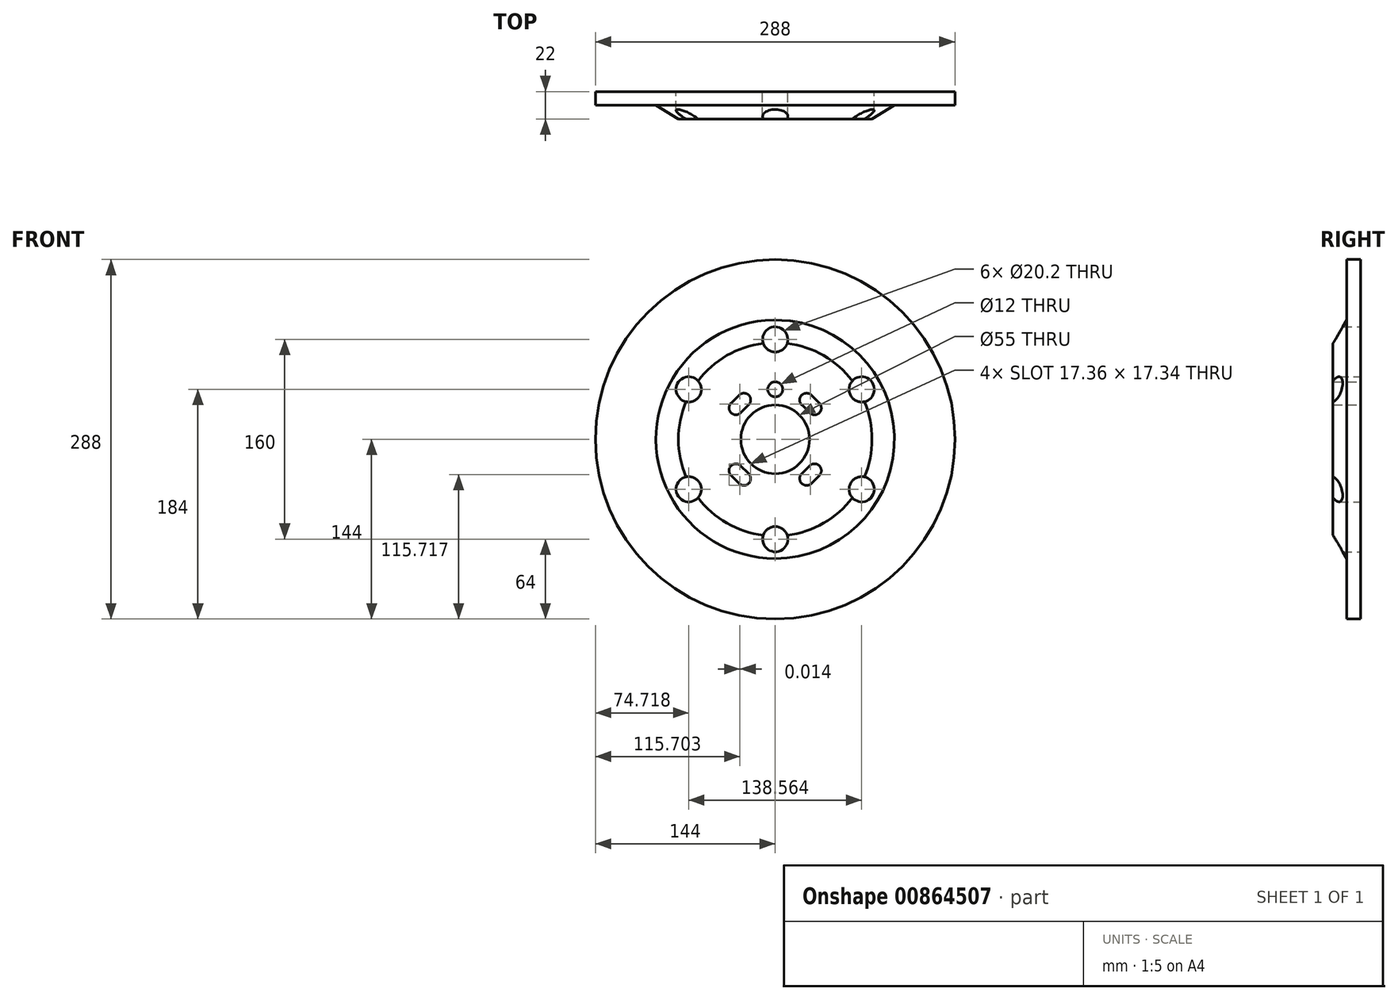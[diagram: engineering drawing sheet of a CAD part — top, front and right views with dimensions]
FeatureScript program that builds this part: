
annotation { "Feature Type Name" : "Feature", "Feature Type Description" : "" }
export const myFeature = defineFeature(function(context is Context, id is Id, definition is map)
    precondition{}
    {
        {
            var Q0;
            Q0=qCreatedBy(makeId("Front.planeOp"),FACE);
            var sketch = newSketch(context, id + "F0", { "sketchPlane" : qUnion([Q0])});
            skCircle(sketch, "E0", {"center": v(0, 0) * mm, "radius": 144 * mm});
            skCircle(sketch, "E1", {"center": v(0, 0) * mm, "radius": 27.5 * mm});
            skCircle(sketch, "E2", {"center": v(0, 80) * mm, "radius": 10.1 * mm});
            skCircle(sketch, "E3.1.0", {"center": v(-69.28, 40) * mm, "radius": 10.1 * mm});
            skCircle(sketch, "E3.2.0", {"center": v(-69.28, -40) * mm, "radius": 10.1 * mm});
            skCircle(sketch, "E3.3.0", {"center": v(0, -80) * mm, "radius": 10.1 * mm});
            skCircle(sketch, "E3.4.0", {"center": v(69.28, -40) * mm, "radius": 10.1 * mm});
            skCircle(sketch, "E3.5.0", {"center": v(69.28, 40) * mm, "radius": 10.1 * mm});
            skCircle(sketch, "E4", {"center": v(0, 40) * mm, "radius": 6 * mm});
            skLineSegment(sketch, "E5", {"start": v(0, 40) * mm, "end": v(9, 40) * mm, "construction": true});
            skLineSegment(sketch, "E6", {"start": v(0, 40) * mm, "end": v(-9, 40) * mm, "construction": true});
            skCircle(sketch, "E7.1.0", {"center": v(-25.1, 31.47) * mm, "radius": 5.5 * mm});
            skLineSegment(sketch, "E7.1.1", {"start": v(-35.35, 29) * mm, "end": v(-29, 35.36) * mm});
            skCircle(sketch, "E7.1.2", {"center": v(-31.47, 25.1) * mm, "radius": 5.5 * mm});
            skLineSegment(sketch, "E7.1.3", {"start": v(-28.15, 20.72) * mm, "end": v(-21.23, 27.56) * mm});
            skCircle(sketch, "E7.3.0", {"center": v(-31.47, -25.1) * mm, "radius": 5.5 * mm});
            skLineSegment(sketch, "E7.3.1", {"start": v(-29, -35.35) * mm, "end": v(-35.36, -29) * mm});
            skCircle(sketch, "E7.3.2", {"center": v(-25.1, -31.47) * mm, "radius": 5.5 * mm});
            skLineSegment(sketch, "E7.3.3", {"start": v(-20.72, -28.15) * mm, "end": v(-27.56, -21.23) * mm});
            skCircle(sketch, "E7.5.0", {"center": v(25.1, -31.47) * mm, "radius": 5.5 * mm});
            skLineSegment(sketch, "E7.5.1", {"start": v(35.35, -29) * mm, "end": v(29, -35.36) * mm});
            skCircle(sketch, "E7.5.2", {"center": v(31.47, -25.1) * mm, "radius": 5.5 * mm});
            skLineSegment(sketch, "E7.5.3", {"start": v(28.15, -20.72) * mm, "end": v(21.23, -27.56) * mm});
            skCircle(sketch, "E7.7.0", {"center": v(31.47, 25.1) * mm, "radius": 5.5 * mm});
            skLineSegment(sketch, "E7.7.1", {"start": v(29, 35.35) * mm, "end": v(35.36, 29) * mm});
            skCircle(sketch, "E7.7.2", {"center": v(25.1, 31.47) * mm, "radius": 5.5 * mm});
            skLineSegment(sketch, "E7.7.3", {"start": v(20.72, 28.15) * mm, "end": v(27.56, 21.23) * mm});
            skCircle(sketch, "E8.cCircle", {"center": v(0, 0) * mm, "radius": 125 * mm, "construction": true});
            skLineSegment(sketch, "E8.0", {"start": v(27.81, 121.86) * mm, "end": v(54.23, 112.61) * mm, "construction": true});
            skLineSegment(sketch, "E8.1", {"start": v(54.23, 112.61) * mm, "end": v(77.93, 97.72) * mm, "construction": true});
            skLineSegment(sketch, "E8.2", {"start": v(77.93, 97.72) * mm, "end": v(97.72, 77.93) * mm, "construction": true});
            skLineSegment(sketch, "E8.3", {"start": v(97.72, 77.93) * mm, "end": v(112.61, 54.23) * mm, "construction": true});
            skLineSegment(sketch, "E8.4", {"start": v(112.61, 54.23) * mm, "end": v(121.86, 27.81) * mm, "construction": true});
            skLineSegment(sketch, "E8.5", {"start": v(121.86, 27.81) * mm, "end": v(124.99, 0) * mm, "construction": true});
            skLineSegment(sketch, "E8.6", {"start": v(125, 0) * mm, "end": v(121.86, -27.81) * mm, "construction": true});
            skLineSegment(sketch, "E8.7", {"start": v(121.86, -27.81) * mm, "end": v(112.61, -54.23) * mm, "construction": true});
            skLineSegment(sketch, "E8.8", {"start": v(112.61, -54.23) * mm, "end": v(97.72, -77.93) * mm, "construction": true});
            skLineSegment(sketch, "E8.9", {"start": v(97.72, -77.93) * mm, "end": v(77.93, -97.72) * mm, "construction": true});
            skLineSegment(sketch, "E8.10", {"start": v(77.93, -97.72) * mm, "end": v(54.23, -112.61) * mm, "construction": true});
            skLineSegment(sketch, "E8.11", {"start": v(54.23, -112.61) * mm, "end": v(27.81, -121.86) * mm, "construction": true});
            skLineSegment(sketch, "E8.12", {"start": v(27.81, -121.86) * mm, "end": v(0, -125) * mm, "construction": true});
            skLineSegment(sketch, "E8.13", {"start": v(0, -125) * mm, "end": v(-27.81, -121.86) * mm, "construction": true});
            skLineSegment(sketch, "E8.14", {"start": v(-27.81, -121.86) * mm, "end": v(-54.23, -112.61) * mm, "construction": true});
            skLineSegment(sketch, "E8.15", {"start": v(-54.23, -112.61) * mm, "end": v(-77.93, -97.72) * mm, "construction": true});
            skLineSegment(sketch, "E8.16", {"start": v(-77.93, -97.72) * mm, "end": v(-97.72, -77.93) * mm, "construction": true});
            skLineSegment(sketch, "E8.17", {"start": v(-97.72, -77.93) * mm, "end": v(-112.61, -54.23) * mm, "construction": true});
            skLineSegment(sketch, "E8.18", {"start": v(-112.61, -54.23) * mm, "end": v(-121.86, -27.81) * mm, "construction": true});
            skLineSegment(sketch, "E8.19", {"start": v(-121.86, -27.81) * mm, "end": v(-124.99, 0) * mm, "construction": true});
            skLineSegment(sketch, "E8.20", {"start": v(-125, 0) * mm, "end": v(-121.86, 27.81) * mm, "construction": true});
            skLineSegment(sketch, "E8.21", {"start": v(-121.86, 27.81) * mm, "end": v(-112.61, 54.23) * mm, "construction": true});
            skLineSegment(sketch, "E8.22", {"start": v(-112.61, 54.23) * mm, "end": v(-97.72, 77.93) * mm, "construction": true});
            skLineSegment(sketch, "E8.23", {"start": v(-97.72, 77.93) * mm, "end": v(-77.93, 97.72) * mm, "construction": true});
            skLineSegment(sketch, "E8.24", {"start": v(-77.93, 97.72) * mm, "end": v(-54.23, 112.61) * mm, "construction": true});
            skLineSegment(sketch, "E8.25", {"start": v(-54.23, 112.61) * mm, "end": v(-27.81, 121.86) * mm, "construction": true});
            skLineSegment(sketch, "E8.26", {"start": v(-27.81, 121.86) * mm, "end": v(0, 125) * mm, "construction": true});
            skLineSegment(sketch, "E8.27", {"start": v(0, 125) * mm, "end": v(27.81, 121.86) * mm, "construction": true});
            skSolve(sketch);
        }
        {
            var Q0;
            Q0=qCreatedBy(makeId("Right.planeOp"),FACE);
            var sketch = newSketch(context, id + "F1", { "sketchPlane" : qUnion([Q0])});
            skLineSegment(sketch, "E9", {"start": v(0, 0) * mm, "end": v(0, 144) * mm});
            skLineSegment(sketch, "E10", {"start": v(0, 144) * mm, "end": v(-11, 144) * mm});
            skLineSegment(sketch, "E11", {"start": v(-11, 144) * mm, "end": v(-11, 95.5) * mm});
            skLineSegment(sketch, "E12", {"start": v(-11, 95.5) * mm, "end": v(-22, 77.5) * mm});
            skLineSegment(sketch, "E13", {"start": v(-22, 77.5) * mm, "end": v(-22, 0) * mm});
            skLineSegment(sketch, "E14", {"start": v(-22, 0) * mm, "end": v(0, 0) * mm});
            skSolve(sketch);
        }
        {
            var Q0;
            Q0=makeQuery(id+"F1.imprint","IMPRINT",FACE,{"disambiguationData":[TD([[makeQuery(id+"F1.imprint","IMPRINT",EDGE,{"derivedFrom":sQuery(id+"F1.wireOp",EDGE,"E9")}),1.0]])]});
            var Q1;
            Q1=sQuery(id+"F1.wireOp",EDGE,"E14");
            revolve(context, id + "F2", {"surfaceOperationType" : NewSurfaceOperationType.NEW, "entities" : qUnion([Q0]), "axis" : qUnion([Q1]), "revolveType" : RevolveType.FULL});
        }
        {
            var Q0;
            Q0=makeQuery(id+"F0.imprint","IMPRINT",FACE,{"disambiguationData":[TD([[makeQuery(id+"F0.imprint","IMPRINT",EDGE,{"derivedFrom":sQuery(id+"F0.wireOp",EDGE,"E0")}),1.0]])]});
            extrude(context, id + "F3", {"entities" : qUnion([Q0]), "operationType" : NewBodyOperationType.INTERSECT, "depth" : 25 * mm, "offsetDistance" : 25 * mm});
        }
    });
